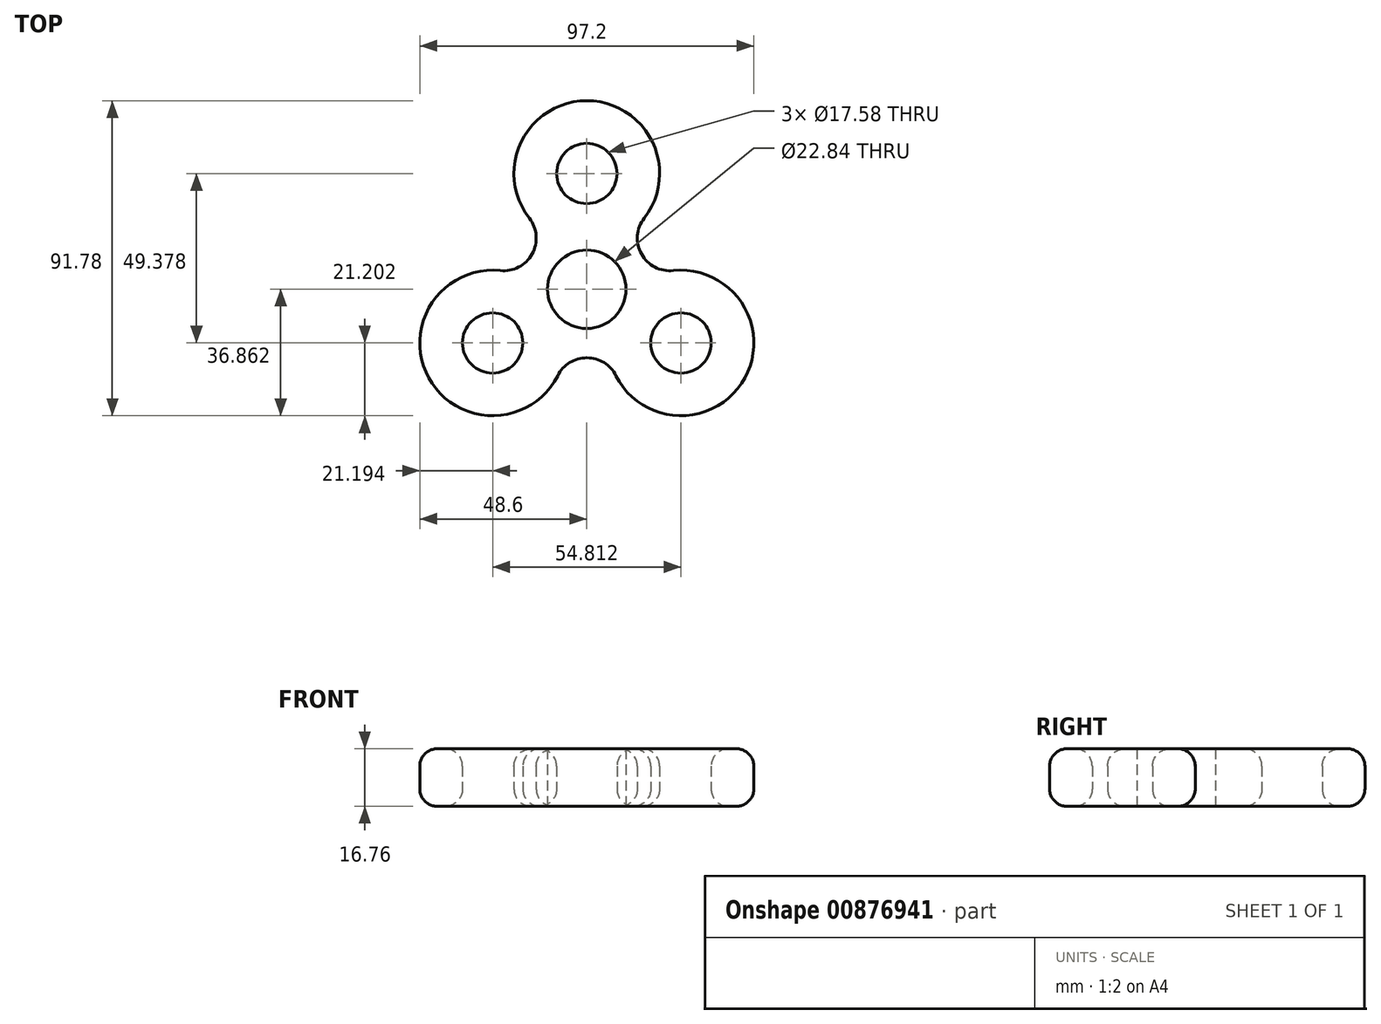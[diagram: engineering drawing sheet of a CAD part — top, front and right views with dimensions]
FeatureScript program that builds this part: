
annotation { "Feature Type Name" : "Feature", "Feature Type Description" : "" }
export const myFeature = defineFeature(function(context is Context, id is Id, definition is map)
    precondition{}
    {
        {
            var Q0;
            Q0=qCreatedBy(makeId("Top.planeOp"),FACE);
            var sketch = newSketch(context, id + "F0", { "sketchPlane" : qUnion([Q0])});
            skArc(sketch, "E0", {"start": v(16.72, 5.83) * mm, "mid": v(0, 40.06) * mm, "end": v(-16.72, 5.83) * mm});
            skArc(sketch, "E1", {"start": v(-25.2, -9.44) * mm, "mid": v(-46.01, -40.68) * mm, "end": v(-8.47, -40.05) * mm});
            skArc(sketch, "E2", {"start": v(8.47, -40.05) * mm, "mid": v(46.01, -40.68) * mm, "end": v(25.2, -9.44) * mm});
            skPoint(sketch, "E3.end.orphan", {"position": v(-21.38, -14.86) * mm});
            skPoint(sketch, "E3.start.orphan", {"position": v(21.38, -14.86) * mm});
            skArc(sketch, "E4", {"start": v(-25.2, -9.44) * mm, "mid": v(-15.91, -4.6) * mm, "end": v(-16.72, 5.83) * mm});
            skArc(sketch, "E5", {"start": v(8.47, -40.05) * mm, "mid": v(0, -34.83) * mm, "end": v(-8.47, -40.05) * mm});
            skPoint(sketch, "E6.orphan", {"position": v(-25.2, -9.44) * mm});
            skArc(sketch, "E7", {"start": v(16.72, 5.83) * mm, "mid": v(15.91, -4.6) * mm, "end": v(25.2, -9.44) * mm});
            skCircle(sketch, "E8", {"center": v(0, 18.86) * mm, "radius": 8.79 * mm});
            skCircle(sketch, "E9", {"center": v(27.4, -30.52) * mm, "radius": 8.79 * mm});
            skCircle(sketch, "E10", {"center": v(-27.4, -30.52) * mm, "radius": 8.79 * mm});
            skCircle(sketch, "E11", {"center": v(0, -14.86) * mm, "radius": 11.42 * mm});
            skSolve(sketch);
        }
        {
            var Q0;
            Q0=makeQuery(id+"F0.imprint","IMPRINT",FACE,{"disambiguationData":[TD([[makeQuery(id+"F0.imprint","IMPRINT",EDGE,{"derivedFrom":sQuery(id+"F0.wireOp",EDGE,"E0")}),1.0]])]});
            extrude(context, id + "F1", {"entities" : qUnion([Q0]), "depth" : 16.76 * mm, "offsetDistance" : 25.4 * mm});
        }
        {
            var Q0;
            Q0=makeQuery(id+"F1.opExtrude","CAP_EDGE",EDGE,{"disambiguationData":[OSD([sQuery(id+"F0.wireOp",EDGE,"E0")])],"isStart":false});
            var Q1;
            Q1=makeQuery(id+"F1.opExtrude","CAP_EDGE",EDGE,{"disambiguationData":[OSD([sQuery(id+"F0.wireOp",EDGE,"E2")])],"isStart":true});
            fillet(context, id + "F2", {"entities" : qUnion([Q0, Q1]), "radius" : 5.08 * mm, "tangentPropagation" : true, "allowEdgeOverflow" : false});
        }
        {
            var Q0;
            Q0=makeQuery(id+"F1.opExtrude","CAP_EDGE",EDGE,{"disambiguationData":[OSD([sQuery(id+"F0.wireOp",EDGE,"E10")])],"isStart":true});
            var Q1;
            Q1=makeQuery(id+"F1.opExtrude","CAP_EDGE",EDGE,{"disambiguationData":[OSD([sQuery(id+"F0.wireOp",EDGE,"E9")])],"isStart":true});
            var Q2;
            Q2=makeQuery(id+"F1.opExtrude","CAP_EDGE",EDGE,{"disambiguationData":[OSD([sQuery(id+"F0.wireOp",EDGE,"E8")])],"isStart":true});
            var Q3;
            Q3=makeQuery(id+"F1.opExtrude","CAP_EDGE",EDGE,{"disambiguationData":[OSD([sQuery(id+"F0.wireOp",EDGE,"E10")])],"isStart":false});
            var Q4;
            Q4=makeQuery(id+"F1.opExtrude","CAP_EDGE",EDGE,{"disambiguationData":[OSD([sQuery(id+"F0.wireOp",EDGE,"E8")])],"isStart":false});
            var Q5;
            Q5=makeQuery(id+"F1.opExtrude","CAP_EDGE",EDGE,{"disambiguationData":[OSD([sQuery(id+"F0.wireOp",EDGE,"E9")])],"isStart":false});
            fillet(context, id + "F3", {"entities" : qUnion([Q0, Q1, Q2, Q3, Q4, Q5]), "radius" : 5.08 * mm, "tangentPropagation" : true, "allowEdgeOverflow" : false});
        }
    });
